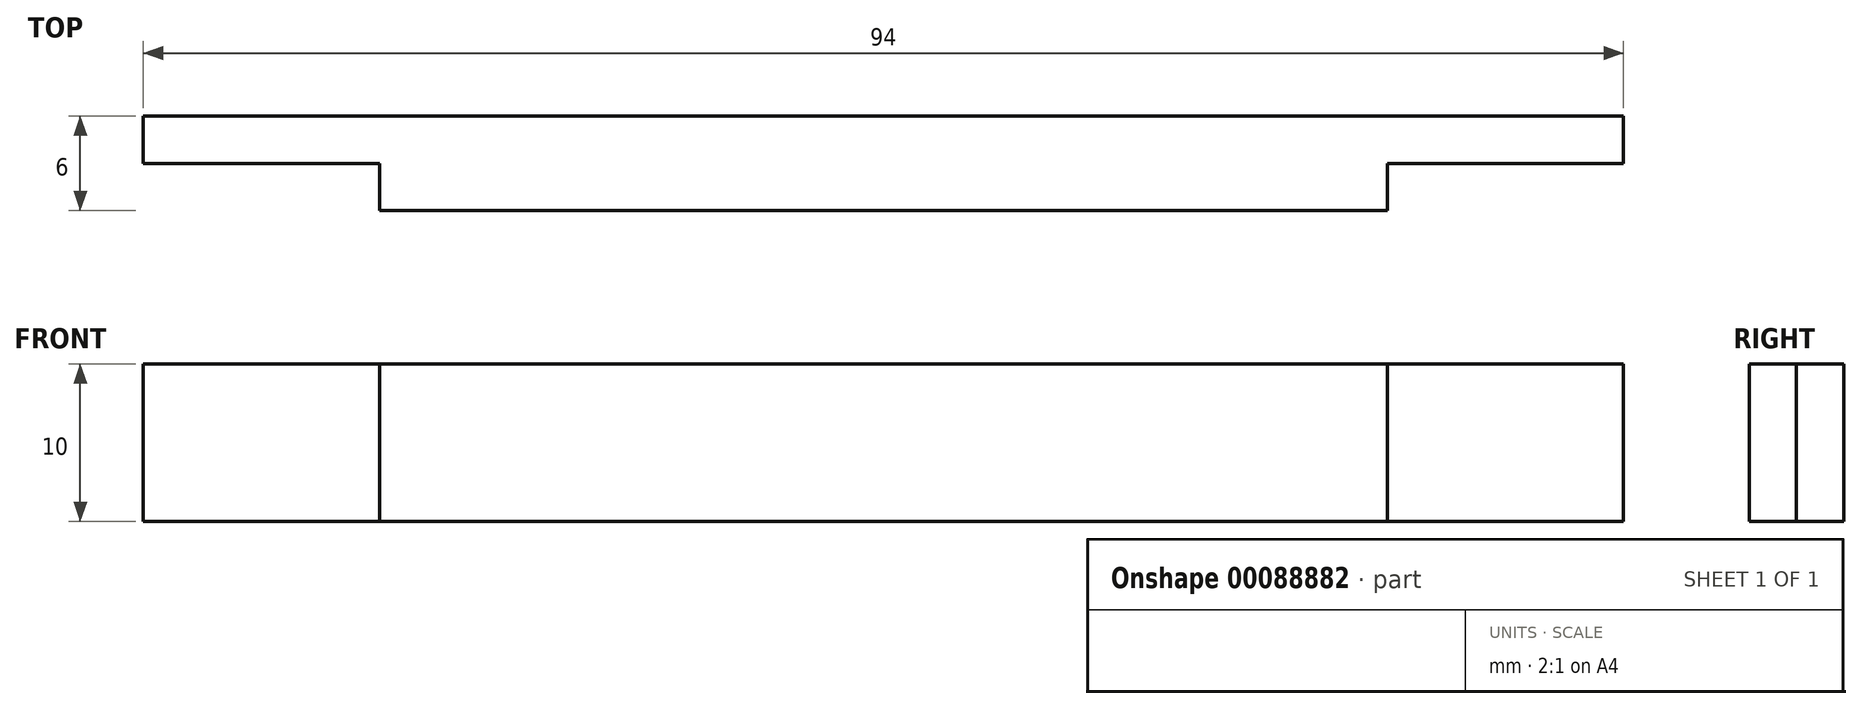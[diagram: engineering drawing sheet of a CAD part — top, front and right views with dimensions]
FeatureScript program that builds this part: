
annotation { "Feature Type Name" : "Feature", "Feature Type Description" : "" }
export const myFeature = defineFeature(function(context is Context, id is Id, definition is map)
    precondition{}
    {
        {
            var Q0;
            Q0=qCreatedBy(makeId("Top.planeOp"),FACE);
            var sketch = newSketch(context, id + "F0", { "sketchPlane" : qUnion([Q0])});
            skLineSegment(sketch, "E0.bottom", {"start": v(47, -3) * mm, "end": v(-47, -3) * mm});
            skLineSegment(sketch, "E0.top", {"start": v(47, 3) * mm, "end": v(-47, 3) * mm});
            skLineSegment(sketch, "E0.left", {"start": v(47, -3) * mm, "end": v(47, 3) * mm});
            skLineSegment(sketch, "E0.right", {"start": v(-47, -3) * mm, "end": v(-47, 3) * mm});
            skPoint(sketch, "E0.middle", {"position": v(0, 0) * mm});
            skSolve(sketch);
        }
        {
            var Q0;
            Q0=qSketchRegion(id+"F0",true);
            extrude(context, id + "F1", {"entities" : qUnion([Q0]), "depth" : 10 * mm});
        }
        {
            var Q0;
            Q0=makeQuery(id+"F1.opExtrude","SWEPT_FACE",FACE,{"disambiguationData":[OSD([sQuery(id+"F0.wireOp",EDGE,"E0.bottom")])]});
            var sketch = newSketch(context, id + "F2", { "sketchPlane" : qUnion([Q0])});
            skLineSegment(sketch, "E1.bottom", {"start": v(47, 10) * mm, "end": v(32, 10) * mm});
            skLineSegment(sketch, "E1.top", {"start": v(47, 0) * mm, "end": v(32, 0) * mm});
            skLineSegment(sketch, "E1.left", {"start": v(47, 10) * mm, "end": v(47, 0) * mm});
            skLineSegment(sketch, "E1.right", {"start": v(32, 10) * mm, "end": v(32, 0) * mm});
            skLineSegment(sketch, "E2.bottom", {"start": v(-47, 10) * mm, "end": v(-32, 10) * mm});
            skLineSegment(sketch, "E2.top", {"start": v(-47, 0) * mm, "end": v(-32, 0) * mm});
            skLineSegment(sketch, "E2.left", {"start": v(-47, 10) * mm, "end": v(-47, 0) * mm});
            skLineSegment(sketch, "E2.right", {"start": v(-32, 10) * mm, "end": v(-32, 0) * mm});
            skSolve(sketch);
        }
        {
            var Q0;
            Q0=qSketchRegion(id+"F2",true);
            extrude(context, id + "F3", {"entities" : qUnion([Q0]), "operationType" : NewBodyOperationType.REMOVE, "oppositeDirection" : true, "depth" : 3 * mm});
        }
    });
